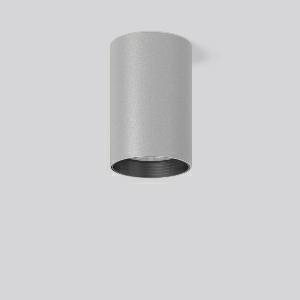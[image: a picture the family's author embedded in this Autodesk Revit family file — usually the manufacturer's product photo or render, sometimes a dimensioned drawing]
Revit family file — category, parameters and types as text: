
# Revit family: heledon_maxi_a_931222_004_3_76_5211
name_source: partatom
category: Lighting Fixtures
units: mm (PartAtom-declared; Revit-internal decimal feet)

## family parameters
Cut with Voids When Loaded = No
Host = Face
Light Source = No
Part Type = Normal
Room Calculation Point = No
Round Connector Dimension = Use Diameter
Shared = No

## types (1)
- HELEDON maxi A (1 x LED Modul 935, 2850 lm, 3500)
    Apparent Load = 25 VA
    Approval mark = CE
    CIE Flux Codes = 96 100 100 100 100
    Color Rendering = 92
    Color Temperature = 3500
    Default Elevation = 1800 mm
    Description = Series: HELEDON maxi
Cylindrical surface-mounted downlight. Housing: die-cast aluminium, powder-coated. Internal ceiling frame polycarbonate with bayonet mounting. Black plastic ring and recessed LED to prevent glare from the side. Optical assembly with lens made of plastic (polycarbonate) for the best homogeneous light distribution - can be changed without tools. Best colour rendering index Ra>90. Suitable for Ceiling mounting. Easy installation with a separate ceiling frame with bayonet mounting and plug connection. Driver integrated. Connected via plug-in connector. High quality converter without flickering and stroboscopic effect. The following accessories can be mounted without use of tools: interchangeable lenses, decorative glasses, honeycomb louvre, clear and frosted diffusers, white interchangeable plastic ring. 
Colour: silver
Diameter: 123 mm
Height: 183 mm
Lamp: LED
Socket: without socket
Colour temperature: 3500K
Colour rendering index (CRI): 92
System power: 25 W
Rated luminous flux: 2850 lm
Luminous efficiency: 114 lm/W
Control gear: Converter, dimmable, DALI
Protection class: I
Type of protection: IP 20
    Height = 183 mm
    Lamp = 1 x LED Modul 935
    Lamp Light Flux = 2850 lm
    Lamp count = 1
    Length = 123 mm
    Lifetime = 50000 h
    Luminous efficacy = 114 lm/W
    Manufacturer = RZB
    ModVariant = No
    Model = 931222.004.3.76
    Mounting Place = Ceiling
    Mounting Type = Surface mounted
    Number of Poles = 1
    OnlyDefault = Yes
    Power Factor = 1
    Product Name = HELEDON maxi A
    Product group = Surface mounted downlights
    ProductGroupID = 302
    Protection Class = Protection class I
    Protection Degree = IP 20
    RLX_Detail_Level = 1
    RLX_Emergency_Light_Flux = 0 lm
    RLX_Emergency_Type = 0
    RLX_Emergency_Type_DB = No
    RlxData = <blob elided: 98197 chars, md5=8c8b4898>
    Socket = socket
    Standby Power = 0 W
    System Light Flux = 2850 lm
    System Power = 25 W
    Type Comments = Product without accessories
    Type Image = 931193.004.jpg
    URL = http://relux.com
    VarID = ---
    Voltage = 230 V
    Voltage Range = 220-240 V
    Weight = 0.00 kg
    Width = 0 mm  [stored 0 ft]

note: [stored X ft] marks values corroborated as IEEE doubles in the binary element streams (Revit-internal decimal feet)

## geometry (parser evidence)
native form markers: Blend x4, Sweep x10
no freeform markers — native parametric forms only
